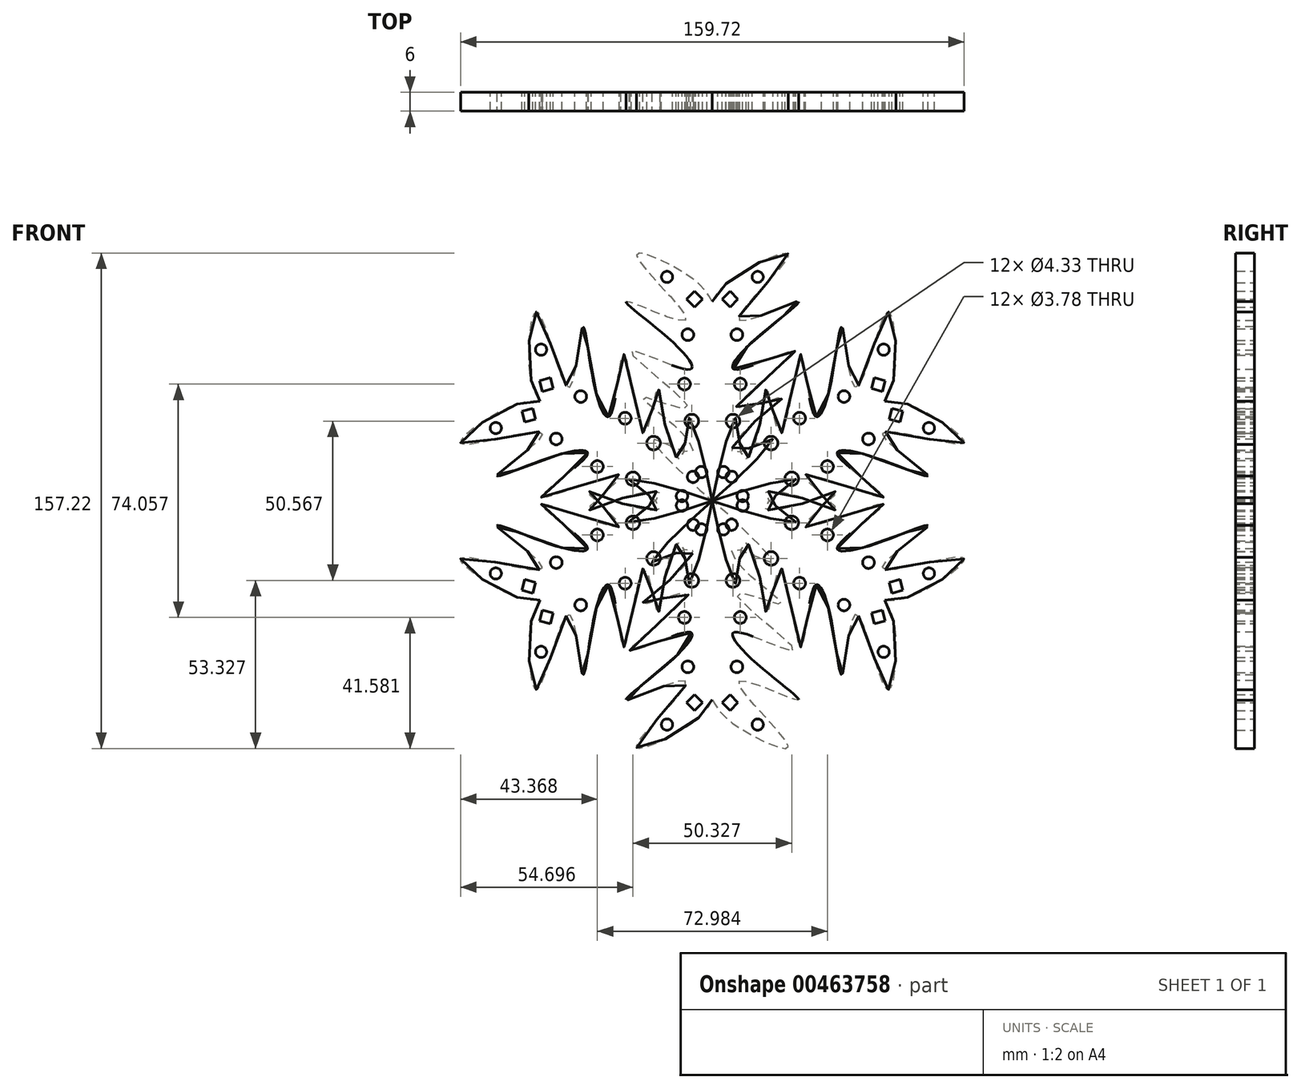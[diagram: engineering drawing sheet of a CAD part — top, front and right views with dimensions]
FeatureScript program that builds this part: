
annotation { "Feature Type Name" : "Feature", "Feature Type Description" : "" }
export const myFeature = defineFeature(function(context is Context, id is Id, definition is map)
    precondition{}
    {
        {
            var Q0;
            Q0=qCreatedBy(makeId("Front.planeOp"),FACE);
            var sketch = newSketch(context, id + "F0", { "sketchPlane" : qUnion([Q0])});
            skLineSegment(sketch, "E0", {"start": v(0, 0) * mm, "end": v(0, 63.17) * mm, "construction": true});
            skFitSpline(sketch, "E1", {"points": [v(0, 63.17) * mm, v(7.42, 71.3) * mm, v(24.08, 77.86) * mm, v(8.37, 57.42) * mm, v(27, 63.22) * mm, v(11.83, 49.64) * mm, v(7.42, 41.63) * mm, v(26.2, 47.51) * mm, v(7.57, 29.4) * mm, v(21.95, 32.87) * mm, v(9.43, 21.42) * mm, v(7.04, 15.3) * mm, v(19.02, 19.55) * mm, v(10.23, 9.44) * mm, v(0, 0) * mm], "startDerivative": vector(78.83, 137.12) * mm, "endDerivative": vector(-207.43, -171.95) * mm});
            skCircle(sketch, "E2", {"center": v(14.37, 71.02) * mm, "radius": 1.79 * mm});
            skCircle(sketch, "E3", {"center": v(7.78, 52.69) * mm, "radius": 1.86 * mm});
            skCircle(sketch, "E4", {"center": v(8.85, 37.03) * mm, "radius": 1.9 * mm});
            skCircle(sketch, "E5", {"center": v(6.54, 25.28) * mm, "radius": 2.16 * mm});
            skCircle(sketch, "E6", {"center": v(3.5, 9.09) * mm, "radius": 1.81 * mm});
            skLineSegment(sketch, "E7.bottom", {"start": v(5.61, 66.53) * mm, "end": v(8.13, 64) * mm});
            skLineSegment(sketch, "E7.top", {"start": v(3.1, 64) * mm, "end": v(5.61, 61.5) * mm});
            skLineSegment(sketch, "E7.left", {"start": v(5.61, 66.53) * mm, "end": v(3.1, 64) * mm});
            skLineSegment(sketch, "E7.right", {"start": v(8.13, 64) * mm, "end": v(5.61, 61.5) * mm});
            skLineSegment(sketch, "E8.MirrorCS", {"start": v(-5.61, 66.53) * mm, "end": v(-3.1, 64) * mm});
            skLineSegment(sketch, "E9.MirrorCS", {"start": v(-3.1, 64) * mm, "end": v(-5.61, 61.5) * mm});
            skLineSegment(sketch, "E10.MirrorCS", {"start": v(-8.13, 64) * mm, "end": v(-5.61, 61.5) * mm});
            skLineSegment(sketch, "E11.MirrorCS", {"start": v(-5.61, 66.53) * mm, "end": v(-8.13, 64) * mm});
            skCircle(sketch, "E12.MirrorC", {"center": v(-14.37, 71.02) * mm, "radius": 1.79 * mm});
            skCircle(sketch, "E13.MirrorC", {"center": v(-8.85, 37.03) * mm, "radius": 1.9 * mm});
            skCircle(sketch, "E14.MirrorC", {"center": v(-3.5, 9.09) * mm, "radius": 1.81 * mm});
            skCircle(sketch, "E15.MirrorC", {"center": v(-7.78, 52.69) * mm, "radius": 1.86 * mm});
            skCircle(sketch, "E16.MirrorC", {"center": v(-6.54, 25.28) * mm, "radius": 2.16 * mm});
            skFitSpline(sketch, "E17.MirrorCS", {"points": [v(0, 63.17) * mm, v(-7.42, 71.3) * mm, v(-24.08, 77.86) * mm, v(-8.37, 57.42) * mm, v(-27, 63.22) * mm, v(-11.83, 49.64) * mm, v(-7.42, 41.63) * mm, v(-26.2, 47.51) * mm, v(-7.57, 29.4) * mm, v(-21.95, 32.87) * mm, v(-9.43, 21.42) * mm, v(-7.04, 15.3) * mm, v(-19.02, 19.55) * mm, v(-10.23, 9.44) * mm, v(0, 0) * mm], "startDerivative": vector(-78.83, 137.12) * mm, "endDerivative": vector(207.43, -171.95) * mm});
            skSolve(sketch);
        }
        {
            var Q0;
            Q0 = qSketchRegion(id + "F0", true);
            extrude(context, id + "F1", {"entities" : qUnion([Q0]), "depth" : 6 * mm});
        }
        {
            var Q0;
            Q0=qCreatedBy(makeId("Right.planeOp"),FACE);
            var sketch = newSketch(context, id + "F2", { "sketchPlane" : qUnion([Q0])});
            skLineSegment(sketch, "E18", {"start": v(0, 0) * mm, "end": v(-43.33, 0) * mm, "construction": true});
            skSolve(sketch);
        }
        {
            var Q0;
            Q0=makeQuery(id+"F1.opExtrude","SWEPT_BODY",BODY,{"disambiguationData":[OSD([sQuery(id+"F0.wireOp",EDGE,"E1"),sQuery(id+"F0.wireOp",EDGE,"E2"),sQuery(id+"F0.wireOp",EDGE,"E3"),sQuery(id+"F0.wireOp",EDGE,"E4"),sQuery(id+"F0.wireOp",EDGE,"E5"),sQuery(id+"F0.wireOp",EDGE,"E6"),sQuery(id+"F0.wireOp",EDGE,"E7.bottom"),sQuery(id+"F0.wireOp",EDGE,"E7.top"),sQuery(id+"F0.wireOp",EDGE,"E7.left"),sQuery(id+"F0.wireOp",EDGE,"E7.right"),sQuery(id+"F0.wireOp",EDGE,"E8.MirrorCS"),sQuery(id+"F0.wireOp",EDGE,"E9.MirrorCS"),sQuery(id+"F0.wireOp",EDGE,"E10.MirrorCS"),sQuery(id+"F0.wireOp",EDGE,"E11.MirrorCS"),sQuery(id+"F0.wireOp",EDGE,"E12.MirrorC"),sQuery(id+"F0.wireOp",EDGE,"E13.MirrorC"),sQuery(id+"F0.wireOp",EDGE,"E14.MirrorC"),sQuery(id+"F0.wireOp",EDGE,"E15.MirrorC"),sQuery(id+"F0.wireOp",EDGE,"E16.MirrorC"),sQuery(id+"F0.wireOp",EDGE,"E17.MirrorCS")])]});
            var Q1;
            Q1=sQuery(id+"F2.wireOp",EDGE,"E18");
            circularPattern(context, id + "F3", {"entities" : qUnion([Q0]), "axis" : qUnion([Q1]), "angle" : 360 * degree, "instanceCount" : 6, "equalSpace" : true});
        }
    });
